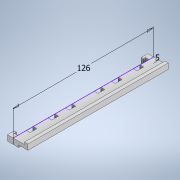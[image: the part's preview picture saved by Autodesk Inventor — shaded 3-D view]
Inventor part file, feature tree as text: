
AUTODESK INVENTOR PART (.ipt)
format: ipt  version: 2022 (Build 260153000, 153)  size: 186,880 bytes
history: native  units: in
note: dims shown in document units (in); Inventor stores cm internally (conversion verified against a paired STEP export)
features: extrude x5, sketch x5
ambient origin geometry x8: Origin, YZ Plane, XZ Plane, XY Plane, X Axis, Y Axis, Z Axis, Center Point
bodies: Solid1 (feature_tree)
feature tree (10):
  extrude  "Extrusion1"  Depth=0.1969in
  extrude  "Extrusion2"  Depth=0.1575in
  extrude  "Extrusion3"  Depth=0.1969in TaperAngle=0.0deg
  extrude  "Extrusion4"  Depth=0.0787in
  extrude  "Extrusion5"  Depth=0.1181in
  sketch  "Sketch1"  dims[d0=4.9606in d1=0.1969in]
  sketch  "Sketch2"  dims[d2=0.1969in d3=0.0in d4=0.1575in]
  sketch  "Sketch3"  dims[d5=0.1575in d6=0.1969in d7=0.0in]
  sketch  "Sketch4"  dims[d8=0.0787in d9=0.0787in]
  sketch  "Sketch5"  dims[d10=0.1969in d11=0.0in d12=0.1181in d13=0.1181in d14=0.0787in d15=0.1969in d16=0.0in d17=0.0in d18=0.2362in d20=0.2362in d21=1.0039in d22=1.0039in d25=0.2362in d26=0.2362in d27=1.7717in d28=1.7717in d29=0.3937in d30=0.0in d31=0.1378in d32=0.1378in d33=0.2362in d34=0.2362in d35=0.3937in d36=0.3937in d37=0.0787in]
